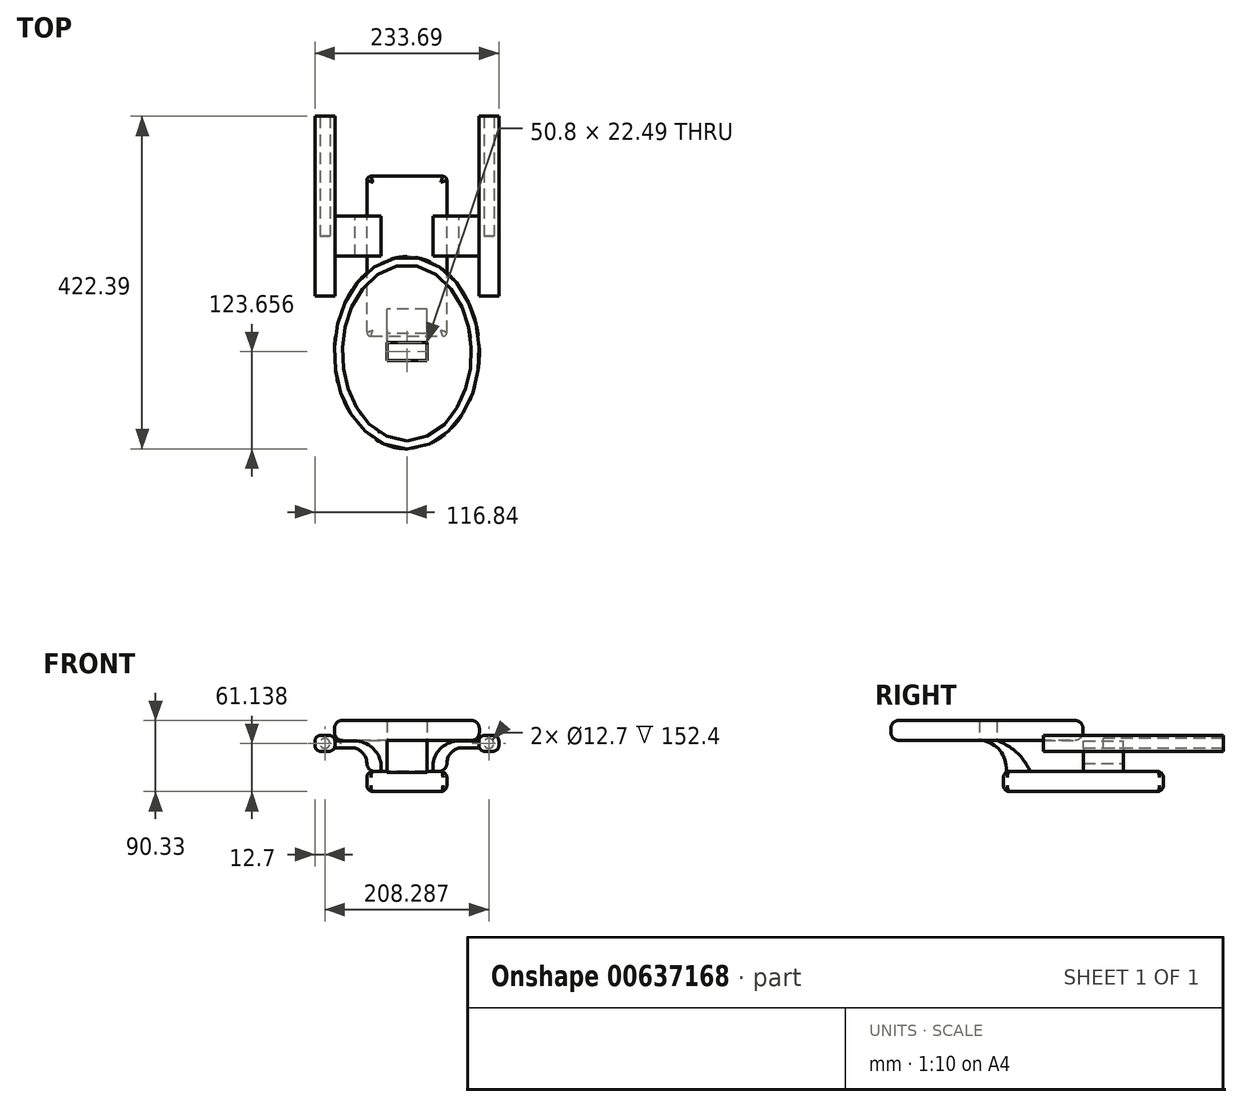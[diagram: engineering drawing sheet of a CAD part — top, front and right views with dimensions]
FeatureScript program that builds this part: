
annotation { "Feature Type Name" : "Feature", "Feature Type Description" : "" }
export const myFeature = defineFeature(function(context is Context, id is Id, definition is map)
    precondition{}
    {
        {
            var Q0;
            Q0=qCreatedBy(makeId("Front.planeOp"),FACE);
            var sketch = newSketch(context, id + "F0", { "sketchPlane" : qUnion([Q0])});
            skLineSegment(sketch, "E0.bottom", {"start": v(-50.8, 12.7) * mm, "end": v(50.8, 12.7) * mm});
            skLineSegment(sketch, "E0.top", {"start": v(-50.8, -12.7) * mm, "end": v(50.8, -12.7) * mm});
            skLineSegment(sketch, "E0.left", {"start": v(-50.8, 12.7) * mm, "end": v(-50.8, -12.7) * mm});
            skLineSegment(sketch, "E0.right", {"start": v(50.8, 12.7) * mm, "end": v(50.8, -12.7) * mm});
            skPoint(sketch, "E0.middle", {"position": v(0, 0) * mm});
            skLineSegment(sketch, "E1.bottom", {"start": v(-91.44, 38.28) * mm, "end": v(-116.84, 38.28) * mm});
            skLineSegment(sketch, "E1.top", {"start": v(-91.44, 58.6) * mm, "end": v(-116.84, 58.6) * mm});
            skLineSegment(sketch, "E1.left", {"start": v(-91.44, 38.28) * mm, "end": v(-91.44, 58.6) * mm});
            skLineSegment(sketch, "E1.right", {"start": v(-116.84, 38.28) * mm, "end": v(-116.84, 58.6) * mm});
            skPoint(sketch, "E1.middle", {"position": v(-104.14, 48.44) * mm});
            skLineSegment(sketch, "E2.bottom", {"start": v(91.45, 38.28) * mm, "end": v(116.85, 38.28) * mm});
            skLineSegment(sketch, "E2.top", {"start": v(91.45, 58.6) * mm, "end": v(116.85, 58.6) * mm});
            skLineSegment(sketch, "E2.left", {"start": v(91.45, 38.28) * mm, "end": v(91.45, 58.6) * mm});
            skLineSegment(sketch, "E2.right", {"start": v(116.85, 38.28) * mm, "end": v(116.85, 58.6) * mm});
            skPoint(sketch, "E2.middle", {"position": v(104.15, 48.44) * mm});
            skPoint(sketch, "E2.middle.positionSnap0", {"position": v(-91.44, 48.44) * mm});
            skPoint(sketch, "E2.centerSnap0", {"position": v(-91.44, 48.44) * mm});
            skLineSegment(sketch, "E3", {"start": v(50.8, 12.7) * mm, "end": v(50.8, 22.86) * mm});
            skLineSegment(sketch, "E4", {"start": v(-50.8, 12.7) * mm, "end": v(-50.8, 22.86) * mm});
            skArc(sketch, "E5", {"start": v(50.8, 22.86) * mm, "mid": v(55.06, 35.3) * mm, "end": v(66.05, 42.5) * mm});
            skLineSegment(sketch, "E6", {"start": v(66.05, 42.5) * mm, "end": v(91.45, 42.5) * mm});
            skArc(sketch, "E7", {"start": v(-50.8, 22.86) * mm, "mid": v(-55.06, 35.29) * mm, "end": v(-66.04, 42.5) * mm});
            skLineSegment(sketch, "E8", {"start": v(-66.04, 42.5) * mm, "end": v(-91.44, 42.38) * mm});
            skLineSegment(sketch, "E9", {"start": v(91.45, 51.35) * mm, "end": v(66.05, 51.35) * mm});
            skArc(sketch, "E10", {"start": v(66.05, 51.35) * mm, "mid": v(44.24, 43.24) * mm, "end": v(33.02, 22.86) * mm});
            skLineSegment(sketch, "E11", {"start": v(33.02, 22.86) * mm, "end": v(33.02, 12.7) * mm});
            skLineSegment(sketch, "E12", {"start": v(-91.44, 51.35) * mm, "end": v(-66.04, 51.35) * mm});
            skArc(sketch, "E13", {"start": v(-66.04, 51.35) * mm, "mid": v(-44.23, 43.24) * mm, "end": v(-33.02, 22.86) * mm});
            skLineSegment(sketch, "E14", {"start": v(-33.02, 22.86) * mm, "end": v(-33.02, 12.7) * mm});
            skSolve(sketch);
        }
        {
            var Q0;
            Q0=makeQuery(id+"F0.imprint","IMPRINT",FACE,{"disambiguationData":[TD([[makeQuery(id+"F0.imprint","IMPRINT",EDGE,{"derivedFrom":sQuery(id+"F0.wireOp",EDGE,"E0.top")}),1.0]])]});
            extrude(context, id + "F1", {"entities" : qUnion([Q0]), "depth" : 127 * mm, "offsetDistance" : 25.4 * mm, "hasSecondDirection" : true, "secondDirectionOppositeDirection" : true, "secondDirectionDepth" : 76.2 * mm});
        }
        {
            var Q0;
            {var subQ3=sQuery(id+"F0.wireOp",EDGE,"E2.bottom");Q0=makeQuery(id+"F0.imprint","IMPRINT",FACE,{"disambiguationData":[TD([[makeQuery(id+"F0.imprint","IMPRINT",EDGE,{"derivedFrom":subQ3}),1.0]])]});}
            extrude(context, id + "F2", {"entities" : qUnion([Q0]), "depth" : 76.2 * mm, "offsetDistance" : 25.4 * mm, "hasSecondDirection" : true, "secondDirectionOppositeDirection" : true, "secondDirectionDepth" : 152.4 * mm});
        }
        {
            var Q0;
            {var subQ3=sQuery(id+"F0.wireOp",EDGE,"E1.bottom");Q0=makeQuery(id+"F0.imprint","IMPRINT",FACE,{"disambiguationData":[TD([[makeQuery(id+"F0.imprint","IMPRINT",EDGE,{"derivedFrom":subQ3}),-1.0]])]});}
            extrude(context, id + "F3", {"entities" : qUnion([Q0]), "depth" : 76.2 * mm, "offsetDistance" : 25.4 * mm, "hasSecondDirection" : true, "secondDirectionOppositeDirection" : true, "secondDirectionDepth" : 152.4 * mm});
        }
        {
            var Q0;
            {var subQ0=sQuery(id+"F0.wireOp",EDGE,"E4");Q0=makeQuery(id+"F0.imprint","IMPRINT",FACE,{"disambiguationData":[TD([[makeQuery(id+"F0.imprint","IMPRINT",EDGE,{"derivedFrom":subQ0}),-1.0]])]});}
            extrude(context, id + "F4", {"entities" : qUnion([Q0]), "depth" : 25.4 * mm, "offsetDistance" : 25.4 * mm, "hasSecondDirection" : true, "secondDirectionOppositeDirection" : true, "secondDirectionDepth" : 25.4 * mm});
        }
        {
            var Q0;
            {var subQ0=sQuery(id+"F0.wireOp",EDGE,"E3");Q0=makeQuery(id+"F0.imprint","IMPRINT",FACE,{"disambiguationData":[TD([[makeQuery(id+"F0.imprint","IMPRINT",EDGE,{"derivedFrom":subQ0}),1.0]])]});}
            extrude(context, id + "F5", {"entities" : qUnion([Q0]), "depth" : 25.4 * mm, "offsetDistance" : 25.4 * mm, "hasSecondDirection" : true, "secondDirectionOppositeDirection" : true, "secondDirectionDepth" : 25.4 * mm});
        }
        {
            var Q0;
            Q0=qCreatedBy(makeId("Right.planeOp"),FACE);
            var sketch = newSketch(context, id + "F6", { "sketchPlane" : qUnion([Q0])});
            skLineSegment(sketch, "E15", {"start": v(-123.49, 12.39) * mm, "end": v(-123.49, 17.47) * mm});
            skArc(sketch, "E16", {"start": v(-123.49, 17.47) * mm, "mid": v(-133.92, 42.3) * mm, "end": v(-158.95, 52.23) * mm});
            skLineSegment(sketch, "E17", {"start": v(-158.95, 52.23) * mm, "end": v(-158.95, 62.4) * mm});
            skFitSpline(sketch, "E18", {"points": [v(-158.95, 62.4) * mm, v(-110.55, 37.49) * mm, v(-92.4, 12.39) * mm], "startDerivative": vector(97.08, -39.51) * mm, "endDerivative": vector(33.03, -61.53) * mm});
            skLineSegment(sketch, "E19", {"start": v(-123.49, 12.39) * mm, "end": v(-92.4, 12.39) * mm});
            skLineSegment(sketch, "E20.bottom", {"start": v(-240.74, 52.23) * mm, "end": v(-77.16, 52.23) * mm});
            skLineSegment(sketch, "E20.top", {"start": v(-240.74, 72.55) * mm, "end": v(-77.16, 72.55) * mm});
            skLineSegment(sketch, "E20.left", {"start": v(-240.74, 52.23) * mm, "end": v(-240.74, 72.55) * mm});
            skLineSegment(sketch, "E20.right", {"start": v(-77.16, 52.23) * mm, "end": v(-77.16, 72.55) * mm});
            skSolve(sketch);
        }
        {
            var Q0;
            {var subQ2=sQuery(id+"F6.wireOp",EDGE,"E15");Q0=makeQuery(id+"F6.imprint","IMPRINT",FACE,{"disambiguationData":[TD([[makeQuery(id+"F6.imprint","IMPRINT",EDGE,{"derivedFrom":subQ2}),-1.0]])]});}
            extrude(context, id + "F7", {"entities" : qUnion([Q0]), "operationType" : NewBodyOperationType.ADD, "endBound" : BoundingType.SYMMETRIC, "depth" : 50.8 * mm, "offsetDistance" : 25.4 * mm});
        }
        {
            var Q0;
            Q0=makeQuery(id+"F7.opExtrude","SWEPT_FACE",FACE,{"disambiguationData":[OSD([sQuery(id+"F6.wireOp",EDGE,"E20.bottom")])]});
            var sketch = newSketch(context, id + "F8", { "sketchPlane" : qUnion([Q0])});
            skEllipse(sketch, "E21", {"center": v(0, -147.96) * mm, "majorRadius": 122.03 * mm, "minorRadius": 92.08 * mm, "majorAxis": v(0, -1)});
            skPoint(sketch, "E21.centerSnap0", {"position": v(0, -157.58) * mm});
            skSolve(sketch);
        }
        {
            var Q0;
            Q0=makeQuery(id+"F8.imprint","IMPRINT",FACE,{"disambiguationData":[TD([[makeQuery(id+"F8.imprint","IMPRINT",EDGE,{"derivedFrom":sQuery(id+"F8.wireOp",EDGE,"E21")}),1.0]])]});
            extrude(context, id + "F9", {"entities" : qUnion([Q0]), "depth" : 25.4 * mm, "offsetDistance" : 25.4 * mm});
        }
        {
            var Q0;
            Q0=makeQuery(id+"F1.opExtrude","CAP_EDGE",EDGE,{"disambiguationData":[OSD([sQuery(id+"F0.wireOp",EDGE,"E0.right")])],"isStart":false});
            var Q1;
            Q1=makeQuery(id+"F1.opExtrude","CAP_EDGE",EDGE,{"disambiguationData":[OSD([sQuery(id+"F0.wireOp",EDGE,"E0.left")])],"isStart":false});
            var Q2;
            Q2=makeQuery(id+"F1.opExtrude","CAP_EDGE",EDGE,{"disambiguationData":[OSD([sQuery(id+"F0.wireOp",EDGE,"E0.right")])],"isStart":true});
            var Q3;
            Q3=makeQuery(id+"F1.opExtrude","CAP_EDGE",EDGE,{"disambiguationData":[OSD([sQuery(id+"F0.wireOp",EDGE,"E0.left")])],"isStart":true});
            fillet(context, id + "F10", {"entities" : qUnion([Q0, Q1, Q2, Q3]), "radius" : 5.08 * mm, "tangentPropagation" : true, "allowEdgeOverflow" : false});
        }
        {
            var Q0;
            Q0=makeQuery(id+"F1.opExtrude","SWEPT_EDGE",EDGE,{"disambiguationData":[OSD([sQuery(id+"F0.wireOp",EDGE,"E0.bottom"),sQuery(id+"F0.wireOp",EDGE,"E0.right"),sQuery(id+"F0.wireOp",EDGE,"E3")])]});
            var Q1;
            Q1=makeQuery(id+"F1.opExtrude","SWEPT_EDGE",EDGE,{"disambiguationData":[OSD([sQuery(id+"F0.wireOp",EDGE,"E0.top"),sQuery(id+"F0.wireOp",EDGE,"E0.right")])]});
            var Q2;
            Q2=makeQuery(id+"F1.opExtrude","SWEPT_EDGE",EDGE,{"disambiguationData":[OSD([sQuery(id+"F0.wireOp",EDGE,"E0.top"),sQuery(id+"F0.wireOp",EDGE,"E0.left")])]});
            var Q3;
            Q3=makeQuery(id+"F1.opExtrude","SWEPT_EDGE",EDGE,{"disambiguationData":[OSD([sQuery(id+"F0.wireOp",EDGE,"E0.bottom"),sQuery(id+"F0.wireOp",EDGE,"E0.left"),sQuery(id+"F0.wireOp",EDGE,"E4")])]});
            fillet(context, id + "F11", {"entities" : qUnion([Q0, Q1, Q2, Q3]), "radius" : 7.62 * mm, "tangentPropagation" : true, "allowEdgeOverflow" : false});
        }
        {
            var Q0;
            Q0=makeQuery(id+"F9.opExtrude","CAP_EDGE",EDGE,{"disambiguationData":[OSD([sQuery(id+"F8.wireOp",EDGE,"E21")])],"isStart":true});
            var Q1;
            Q1=makeQuery(id+"F9.opExtrude","CAP_EDGE",EDGE,{"disambiguationData":[OSD([sQuery(id+"F8.wireOp",EDGE,"E21")])],"isStart":false});
            fillet(context, id + "F12", {"entities" : qUnion([Q0, Q1]), "radius" : 10.16 * mm, "tangentPropagation" : true, "allowEdgeOverflow" : false});
        }
        {
            var Q0;
            Q0=makeQuery(id+"F2.opExtrude","SWEPT_EDGE",EDGE,{"disambiguationData":[OSD([sQuery(id+"F0.wireOp",EDGE,"E2.top"),sQuery(id+"F0.wireOp",EDGE,"E2.right")])]});
            var Q1;
            Q1=makeQuery(id+"F2.opExtrude","SWEPT_EDGE",EDGE,{"disambiguationData":[OSD([sQuery(id+"F0.wireOp",EDGE,"E2.top"),sQuery(id+"F0.wireOp",EDGE,"E2.left")])]});
            var Q2;
            Q2=makeQuery(id+"F2.opExtrude","SWEPT_EDGE",EDGE,{"disambiguationData":[OSD([sQuery(id+"F0.wireOp",EDGE,"E2.bottom"),sQuery(id+"F0.wireOp",EDGE,"E2.left")])]});
            var Q3;
            Q3=makeQuery(id+"F3.opExtrude","SWEPT_EDGE",EDGE,{"disambiguationData":[OSD([sQuery(id+"F0.wireOp",EDGE,"E1.top"),sQuery(id+"F0.wireOp",EDGE,"E1.left")])]});
            var Q4;
            Q4=makeQuery(id+"F3.opExtrude","SWEPT_EDGE",EDGE,{"disambiguationData":[OSD([sQuery(id+"F0.wireOp",EDGE,"E1.top"),sQuery(id+"F0.wireOp",EDGE,"E1.right")])]});
            var Q5;
            Q5=makeQuery(id+"F3.opExtrude","SWEPT_EDGE",EDGE,{"disambiguationData":[OSD([sQuery(id+"F0.wireOp",EDGE,"E1.bottom"),sQuery(id+"F0.wireOp",EDGE,"E1.right")])]});
            var Q6;
            Q6=makeQuery(id+"F3.opExtrude","SWEPT_EDGE",EDGE,{"disambiguationData":[OSD([sQuery(id+"F0.wireOp",EDGE,"E1.bottom"),sQuery(id+"F0.wireOp",EDGE,"E1.left")])]});
            var Q7;
            Q7=makeQuery(id+"F2.opExtrude","SWEPT_EDGE",EDGE,{"disambiguationData":[OSD([sQuery(id+"F0.wireOp",EDGE,"E2.bottom"),sQuery(id+"F0.wireOp",EDGE,"E2.right")])]});
            fillet(context, id + "F13", {"entities" : qUnion([Q0, Q1, Q2, Q3, Q4, Q5, Q6, Q7]), "radius" : 7.62 * mm, "tangentPropagation" : true, "allowEdgeOverflow" : false});
        }
        {
            var Q0;
            Q0=makeQuery(id+"F5.opExtrude","SWEPT_EDGE",EDGE,{"disambiguationData":[OSD([sQuery(id+"F0.wireOp",EDGE,"E0.bottom"),sQuery(id+"F0.wireOp",EDGE,"E0.right"),sQuery(id+"F0.wireOp",EDGE,"E3")])]});
            var Q1;
            Q1=makeQuery(id+"F4.opExtrude","SWEPT_EDGE",EDGE,{"disambiguationData":[OSD([sQuery(id+"F0.wireOp",EDGE,"E0.bottom"),sQuery(id+"F0.wireOp",EDGE,"E0.left"),sQuery(id+"F0.wireOp",EDGE,"E4")])]});
            fillet(context, id + "F14", {"entities" : qUnion([Q0, Q1]), "radius" : 10.16 * mm, "tangentPropagation" : true, "allowEdgeOverflow" : false});
        }
        {
            var Q0;
            Q0=sQuery(id+"F0.wireOp",VERTEX,"E1.middle");
            var Q1;
            Q1=makeQuery(id+"F3.opExtrude","SWEPT_BODY",BODY,{"disambiguationData":[OSD([sQuery(id+"F0.wireOp",EDGE,"E1.bottom"),sQuery(id+"F0.wireOp",EDGE,"E1.top"),sQuery(id+"F0.wireOp",EDGE,"E1.left"),sQuery(id+"F0.wireOp",EDGE,"E1.right")])]});
            hole(context, id + "F15", {"style" : HoleStyle.SIMPLE, "endStyle" : HoleEndStyle.THROUGH, "holeDiameter" : 12.7 * mm, "majorDiameter" : 6.35 * mm, "isTappedThrough" : true, "tappedDepth" : 12.7 * mm, "tapClearance" : 3, "locations" : qUnion([Q0]), "scope" : qUnion([Q1])});
        }
        {
            var Q0;
            Q0=sQuery(id+"F0.wireOp",VERTEX,"E2.middle");
            var Q1;
            Q1=makeQuery(id+"F2.opExtrude","SWEPT_BODY",BODY,{"disambiguationData":[OSD([sQuery(id+"F0.wireOp",EDGE,"E2.bottom"),sQuery(id+"F0.wireOp",EDGE,"E2.top"),sQuery(id+"F0.wireOp",EDGE,"E2.left"),sQuery(id+"F0.wireOp",EDGE,"E2.right")])]});
            hole(context, id + "F16", {"style" : HoleStyle.SIMPLE, "endStyle" : HoleEndStyle.THROUGH, "holeDiameter" : 12.7 * mm, "majorDiameter" : 6.35 * mm, "isTappedThrough" : true, "tappedDepth" : 12.7 * mm, "tapClearance" : 3, "locations" : qUnion([Q0]), "scope" : qUnion([Q1])});
        }
    });
